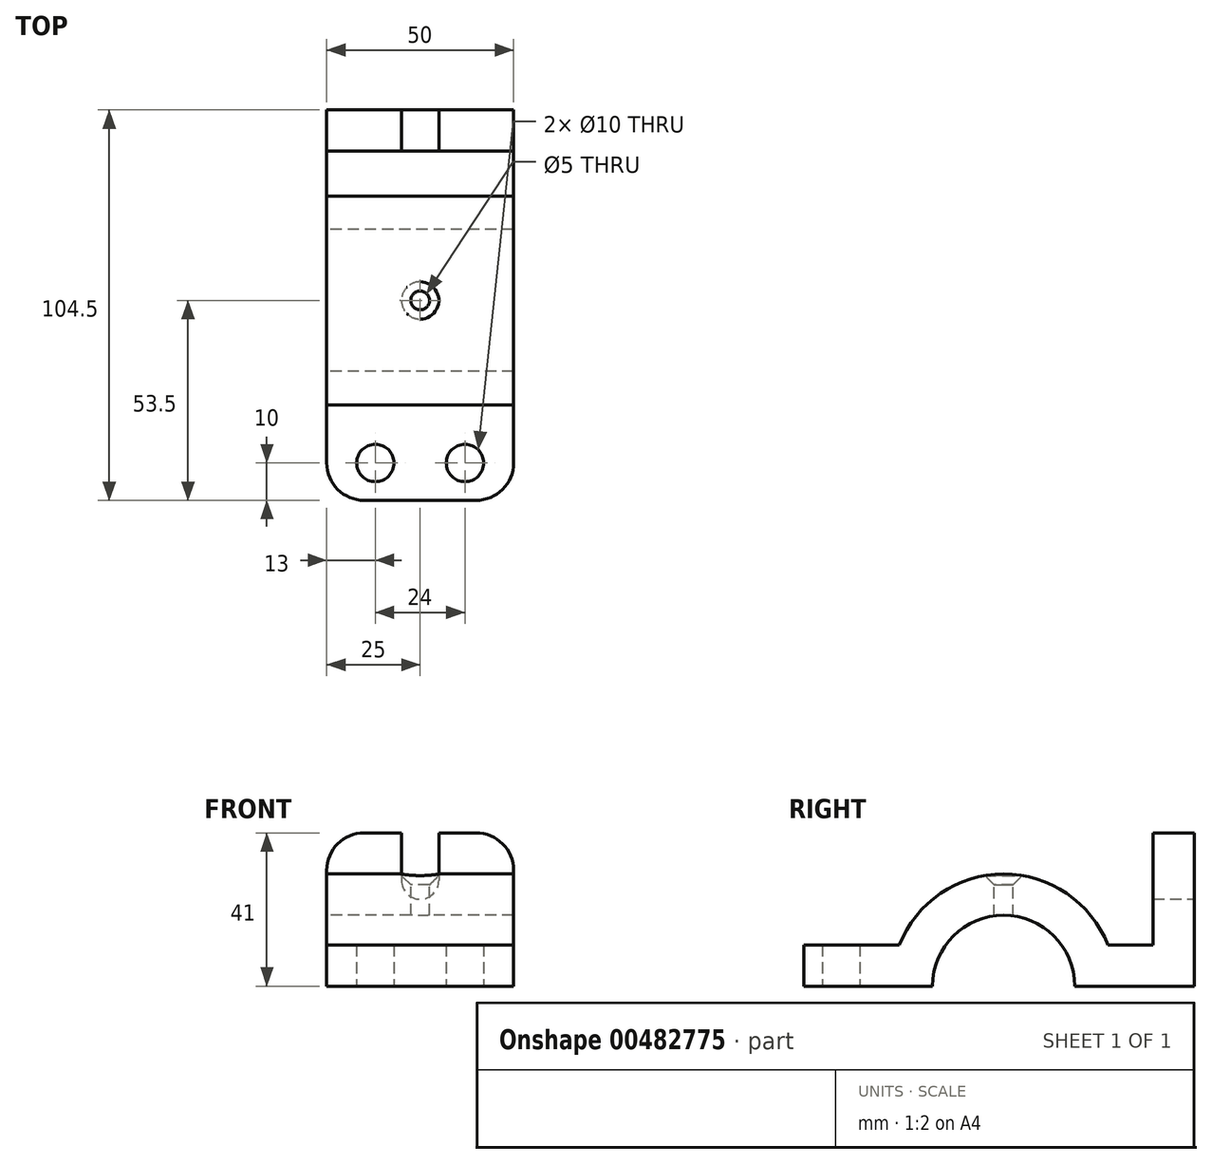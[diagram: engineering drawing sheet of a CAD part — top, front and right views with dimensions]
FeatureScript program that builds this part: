
annotation { "Feature Type Name" : "Feature", "Feature Type Description" : "" }
export const myFeature = defineFeature(function(context is Context, id is Id, definition is map)
    precondition{}
    {
        {
            var Q0;
            Q0=qCreatedBy(makeId("Right.planeOp"),FACE);
            var sketch = newSketch(context, id + "F0", { "sketchPlane" : qUnion([Q0])});
            skLineSegment(sketch, "E0", {"start": v(-53.5, 11) * mm, "end": v(-27.91, 11) * mm});
            skLineSegment(sketch, "E1", {"start": v(40, 11) * mm, "end": v(40, 41) * mm});
            skLineSegment(sketch, "E2", {"start": v(40, 41) * mm, "end": v(51, 41) * mm});
            skLineSegment(sketch, "E3", {"start": v(51, 41) * mm, "end": v(51, 0) * mm});
            skLineSegment(sketch, "E4", {"start": v(51, 0) * mm, "end": v(19, 0) * mm});
            skLineSegment(sketch, "E5", {"start": v(-53.5, 0) * mm, "end": v(-53.5, 11) * mm});
            skLineSegment(sketch, "E6", {"start": v(40, 11) * mm, "end": v(51, 11) * mm});
            skArc(sketch, "E7", {"start": v(19, 0) * mm, "mid": v(0, 19) * mm, "end": v(-19, 0) * mm});
            skArc(sketch, "E8", {"start": v(30, 0) * mm, "mid": v(0, 30) * mm, "end": v(-30, 0) * mm});
            skLineSegment(sketch, "E9.trimOffspring", {"start": v(-19, 0) * mm, "end": v(-53.5, 0) * mm});
            skLineSegment(sketch, "E10.trimOffspring", {"start": v(27.91, 11) * mm, "end": v(40, 11) * mm});
            skSolve(sketch);
        }
        {
            var Q0;
            Q0 = qSketchRegion(id + "F0", true);
            extrude(context, id + "F1", {"entities" : qUnion([Q0]), "depth" : 25 * mm, "hasSecondDirection" : true, "secondDirectionOppositeDirection" : true, "secondDirectionDepth" : 25 * mm});
        }
        {
            var Q0;
            Q0=makeQuery(id+"F1.opExtrude","SWEPT_FACE",FACE,{"disambiguationData":[OSD([sQuery(id+"F0.wireOp",EDGE,"E3")])]});
            var sketch = newSketch(context, id + "F2", { "sketchPlane" : qUnion([Q0])});
            skLineSegment(sketch, "E11.bottom", {"start": v(-5, 41) * mm, "end": v(5, 41) * mm});
            skLineSegment(sketch, "E11.top", {"start": v(-5, 28.27) * mm, "end": v(5, 28.27) * mm});
            skLineSegment(sketch, "E11.left", {"start": v(-5, 41) * mm, "end": v(-5, 28.27) * mm});
            skLineSegment(sketch, "E11.right", {"start": v(5, 41) * mm, "end": v(5, 28.27) * mm});
            skCircle(sketch, "E12", {"center": v(0, 28.27) * mm, "radius": 5 * mm});
            skSolve(sketch);
        }
        {
            var Q0;
            Q0 = qSketchRegion(id + "F2", true);
            extrude(context, id + "F3", {"entities" : qUnion([Q0]), "operationType" : NewBodyOperationType.REMOVE, "oppositeDirection" : true, "depth" : 11 * mm});
        }
        {
            var Q0;
            Q0=makeQuery(id+"F1.opExtrude","CAP_EDGE",EDGE,{"disambiguationData":[OSD([sQuery(id+"F0.wireOp",EDGE,"E5")])],"isStart":false});
            var Q1;
            Q1=makeQuery(id+"F1.opExtrude","CAP_EDGE",EDGE,{"disambiguationData":[OSD([sQuery(id+"F0.wireOp",EDGE,"E5")])],"isStart":true});
            var Q2;
            Q2=makeQuery(id+"F1.opExtrude","CAP_EDGE",EDGE,{"disambiguationData":[OSD([sQuery(id+"F0.wireOp",EDGE,"E2")])],"isStart":false});
            var Q3;
            Q3=makeQuery(id+"F1.opExtrude","CAP_EDGE",EDGE,{"disambiguationData":[OSD([sQuery(id+"F0.wireOp",EDGE,"E2")])],"isStart":true});
            fillet(context, id + "F4", {"entities" : qUnion([Q0, Q1, Q2, Q3]), "radius" : 10 * mm, "tangentPropagation" : true, "allowEdgeOverflow" : false});
        }
        {
            var Q0;
            {var subQ0=sQuery(id+"F0.wireOp",EDGE,"E4");Q0=makeQuery(id+"F1.opExtrude","SWEPT_FACE",FACE,{"disambiguationData":[OSD([subQ0]),TDD([makeQuery(id+"F0.imprint","IMPRINT",EDGE,{"disambiguationData":[TD([[makeQuery(id+"F0.imprint","INTERSECT",VERTEX,{"derivedFrom":[subQ0,sQuery(id+"F0.wireOp",EDGE,"E5")]}),1.0]])],"derivedFrom":subQ0})])]});}
            var sketch = newSketch(context, id + "F5", { "sketchPlane" : qUnion([Q0])});
            skCircle(sketch, "E13", {"center": v(-12, 43.5) * mm, "radius": 5 * mm});
            skCircle(sketch, "E14", {"center": v(12, 43.5) * mm, "radius": 5 * mm});
            skCircle(sketch, "E15", {"center": v(0, 0) * mm, "radius": 2.5 * mm, "construction": true});
            skSolve(sketch);
        }
        {
            var Q0;
            Q0 = qSketchRegion(id + "F5", true);
            extrude(context, id + "F6", {"entities" : qUnion([Q0]), "operationType" : NewBodyOperationType.REMOVE, "oppositeDirection" : true, "depth" : 12 * mm});
        }
        {
            var Q0;
            {var subQ1=sQuery(id+"F0.wireOp",EDGE,"E2");Q0=makeQuery(id+"F3.boolean.opBoolean","SPLIT",FACE,{"disambiguationData":[TD([makeQuery(id+"F3.opExtrude","SWEPT_FACE",FACE,{"disambiguationData":[OSD([sQuery(id+"F2.wireOp",EDGE,"E11.right")])]})])],"derivedFrom":makeQuery(id+"F1.opExtrude","SWEPT_FACE",FACE,{"disambiguationData":[OSD([subQ1])]})});}
            var sketch = newSketch(context, id + "F7", { "sketchPlane" : qUnion([Q0])});
            skCircle(sketch, "E16", {"center": v(0, 0) * mm, "radius": 0.5 * mm});
            skSolve(sketch);
        }
        {
            var Q0;
            Q0=sQuery(id+"F7.wireOp",VERTEX,"E16.center");
            var Q1;
            Q1=makeQuery(id+"F1.opExtrude","SWEPT_BODY",BODY,{"disambiguationData":[OSD([sQuery(id+"F0.wireOp",EDGE,"E0"),sQuery(id+"F0.wireOp",EDGE,"E1"),sQuery(id+"F0.wireOp",EDGE,"E2"),sQuery(id+"F0.wireOp",EDGE,"E3"),sQuery(id+"F0.wireOp",EDGE,"E4"),sQuery(id+"F0.wireOp",EDGE,"E5"),sQuery(id+"F0.wireOp",EDGE,"E7"),sQuery(id+"F0.wireOp",EDGE,"E8")])]});
            hole(context, id + "F8", {"style" : HoleStyle.C_SINK, "endStyle" : HoleEndStyle.THROUGH, "holeDiameter" : 5 * mm, "cSinkDiameter" : 10 * mm, "cSinkAngle" : 90 * degree, "tappedDepth" : 12 * mm, "tapClearance" : 3, "locations" : qUnion([Q0]), "scope" : qUnion([Q1])});
        }
    });
